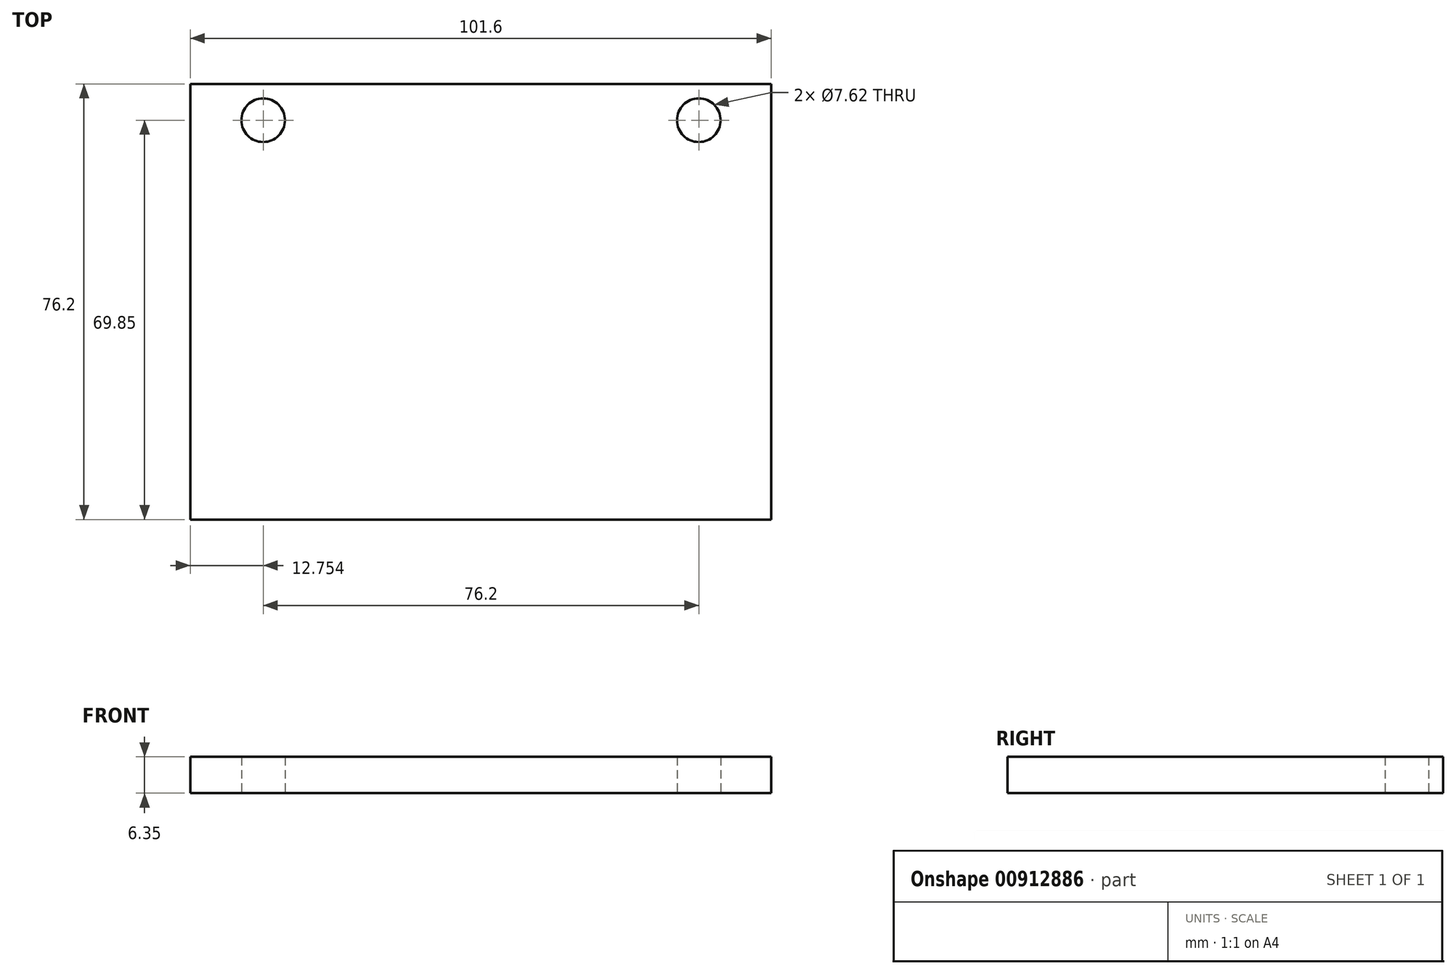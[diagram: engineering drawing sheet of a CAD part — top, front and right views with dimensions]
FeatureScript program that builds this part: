
annotation { "Feature Type Name" : "Feature", "Feature Type Description" : "" }
export const myFeature = defineFeature(function(context is Context, id is Id, definition is map)
    precondition{}
    {
        {
            var Q0;
            Q0=qCreatedBy(makeId("Top.planeOp"),FACE);
            var sketch = newSketch(context, id + "F0", { "sketchPlane" : qUnion([Q0])});
            skLineSegment(sketch, "E0.bottom", {"start": v(50.8, 38.1) * mm, "end": v(-50.8, 38.1) * mm});
            skLineSegment(sketch, "E0.top", {"start": v(50.8, -38.1) * mm, "end": v(-50.8, -38.1) * mm});
            skLineSegment(sketch, "E0.left", {"start": v(50.8, 38.1) * mm, "end": v(50.8, -38.1) * mm});
            skLineSegment(sketch, "E0.right", {"start": v(-50.8, 38.1) * mm, "end": v(-50.8, -38.1) * mm});
            skPoint(sketch, "E0.middle", {"position": v(0, 0) * mm});
            skSolve(sketch);
        }
        {
            var Q0;
            Q0=qCreatedBy(makeId("Top.planeOp"),FACE);
            var sketch = newSketch(context, id + "F1", { "sketchPlane" : qUnion([Q0])});
            skLineSegment(sketch, "E1", {"start": v(-50.75, 31.75) * mm, "end": v(50.85, 31.75) * mm, "construction": true});
            skCircle(sketch, "E2", {"center": v(38.15, 31.75) * mm, "radius": 3.81 * mm});
            skCircle(sketch, "E3", {"center": v(-38.05, 31.75) * mm, "radius": 3.81 * mm});
            skSolve(sketch);
        }
        {
            var Q0;
            Q0 = qSketchRegion(id + "F0", true);
            extrude(context, id + "F2", {"entities" : qUnion([Q0]), "depth" : 6.35 * mm, "offsetDistance" : 25.4 * mm});
        }
        {
            var Q0;
            Q0 = qSketchRegion(id + "F1", true);
            extrude(context, id + "F3", {"entities" : qUnion([Q0]), "operationType" : NewBodyOperationType.REMOVE, "endBound" : BoundingType.THROUGH_ALL, "depth" : 0 * mm, "offsetDistance" : 25.4 * mm});
        }
    });
